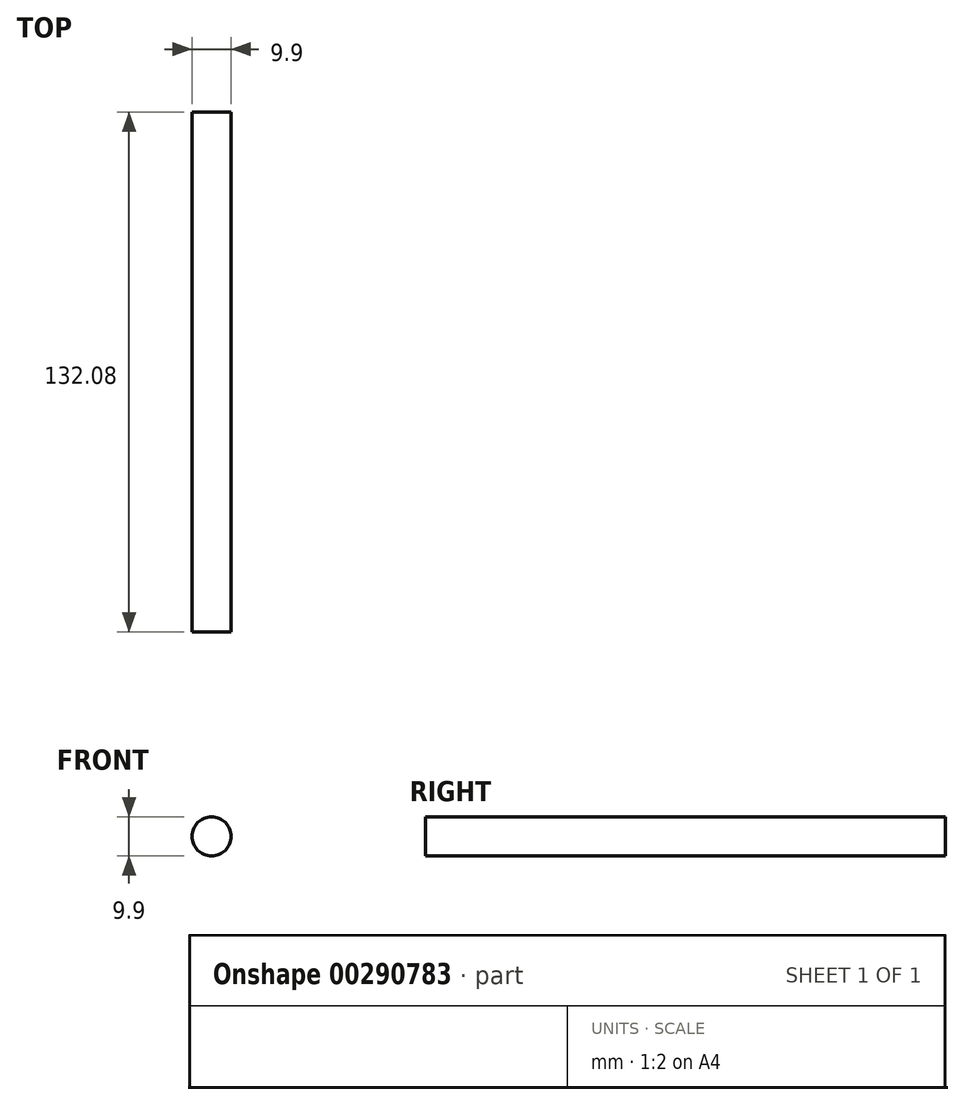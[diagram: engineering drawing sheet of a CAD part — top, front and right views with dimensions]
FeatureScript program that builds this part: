
annotation { "Feature Type Name" : "Feature", "Feature Type Description" : "" }
export const myFeature = defineFeature(function(context is Context, id is Id, definition is map)
    precondition{}
    {
        {
            var Q0;
            Q0=qCreatedBy(makeId("Front.planeOp"),FACE);
            var sketch = newSketch(context, id + "F0", { "sketchPlane" : qUnion([Q0])});
            skCircle(sketch, "E0", {"center": v(0, 0) * mm, "radius": 4.95 * mm});
            skSolve(sketch);
        }
        {
            var Q0;
            Q0 = qSketchRegion(id + "F0", true);
            extrude(context, id + "F1", {"entities" : qUnion([Q0]), "depth" : 132.08 * mm});
        }
    });
